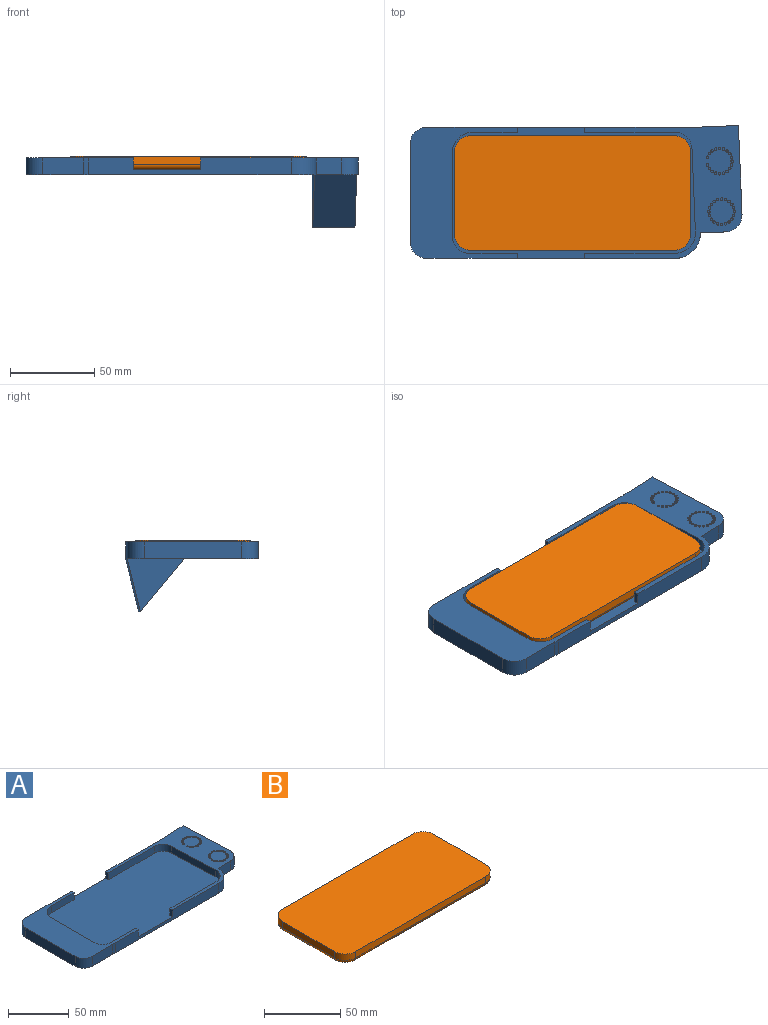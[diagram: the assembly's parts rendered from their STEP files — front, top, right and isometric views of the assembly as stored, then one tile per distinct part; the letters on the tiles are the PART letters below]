
ASSEMBLY  parts=2 mates=1
PART A: 118 faces, bbox 196.6x78.7x41.5 mm
  f0: cylinder r=0.75mm len=2mm, axis (0,0,1), area 9.4mm2, adj f1,f81
  f1: plane 1.5x1.5mm, normal (0,0,1), area 1.8mm2, adj f0
  f2: cylinder r=0.75mm len=2mm, axis (0,0,1), area 9.4mm2, adj f3,f81
  f3: plane 1.5x1.5mm, normal (0,0,1), area 1.8mm2, adj f2
  f4: cylinder r=0.75mm len=2mm, axis (0,0,1), area 9.4mm2, adj f5,f81
  f5: plane 1.5x1.5mm, normal (0,0,1), area 1.8mm2, adj f4
  f6: cylinder r=0.75mm len=2mm, axis (0,0,1), area 9.4mm2, adj f7,f81
  f7: plane 1.5x1.5mm, normal (0,0,1), area 1.8mm2, adj f6
  f8: cylinder r=0.75mm len=2mm, axis (0,0,1), area 9.4mm2, adj f9,f81
  f9: plane 1.5x1.5mm, normal (0,0,1), area 1.8mm2, adj f8
  f10: cylinder r=0.75mm len=2mm, axis (0,0,1), area 9.4mm2, adj f11,f81
  f11: plane 1.5x1.5mm, normal (0,0,1), area 1.8mm2, adj f10
  f12: cylinder r=0.75mm len=2mm, axis (0,0,1), area 9.4mm2, adj f13,f81
  f13: plane 1.5x1.5mm, normal (0,0,1), area 1.8mm2, adj f12
  f14: cylinder r=0.75mm len=2mm, axis (0,0,1), area 9.4mm2, adj f15,f81
  f15: plane 1.5x1.5mm, normal (0,0,1), area 1.8mm2, adj f14
  f16: cylinder r=0.75mm len=2mm, axis (0,0,1), area 9.4mm2, adj f17,f81
  f17: plane 1.5x1.5mm, normal (0,0,1), area 1.8mm2, adj f16
  f18: cylinder r=0.75mm len=2mm, axis (0,0,1), area 9.4mm2, adj f19,f81
  f19: plane 1.5x1.5mm, normal (0,0,1), area 1.8mm2, adj f18
  f20: cylinder r=0.75mm len=2mm, axis (0,0,1), area 9.4mm2, adj f21,f81
  f21: plane 1.5x1.5mm, normal (0,0,1), area 1.8mm2, adj f20
  f22: cylinder r=0.75mm len=2mm, axis (0,0,1), area 9.4mm2, adj f23,f81
  f23: plane 1.5x1.5mm, normal (0,0,1), area 1.8mm2, adj f22
  f24: cylinder r=0.75mm len=2mm, axis (0,0,1), area 9.4mm2, adj f25,f81
  f25: plane 1.5x1.5mm, normal (0,0,1), area 1.8mm2, adj f24
  f26: cylinder r=0.75mm len=2mm, axis (0,0,1), area 9.4mm2, adj f27,f81
  f27: plane 1.5x1.5mm, normal (0,0,1), area 1.8mm2, adj f26
  f28: cylinder r=0.75mm len=2mm, axis (0,0,1), area 9.4mm2, adj f29,f81
  f29: plane 1.5x1.5mm, normal (0,0,1), area 1.8mm2, adj f28
  f30: cylinder r=0.75mm len=2mm, axis (0,0,1), area 9.4mm2, adj f31,f81
  f31: plane 1.5x1.5mm, normal (0,0,1), area 1.8mm2, adj f30
  f32: cylinder r=0.75mm len=2mm, axis (0,0,1), area 9.4mm2, adj f33,f81
  f33: plane 1.5x1.5mm, normal (0,0,1), area 1.8mm2, adj f32
  f34: cylinder r=0.75mm len=2mm, axis (0,0,1), area 9.4mm2, adj f35,f81
  f35: plane 1.5x1.5mm, normal (0,0,1), area 1.8mm2, adj f34
  f36: cylinder r=0.75mm len=2mm, axis (0,0,1), area 9.4mm2, adj f37,f81
  f37: plane 1.5x1.5mm, normal (0,0,1), area 1.8mm2, adj f36
  f38: cylinder r=0.75mm len=2mm, axis (0,0,1), area 9.4mm2, adj f39,f81
  f39: plane 1.5x1.5mm, normal (0,0,1), area 1.8mm2, adj f38
  f40: cylinder r=0.75mm len=2mm, axis (0,0,1), area 9.4mm2, adj f41,f81
  f41: plane 1.5x1.5mm, normal (0,0,1), area 1.8mm2, adj f40
  f42: cylinder r=0.75mm len=2mm, axis (0,0,1), area 9.4mm2, adj f43,f81
  f43: plane 1.5x1.5mm, normal (0,0,1), area 1.8mm2, adj f42
  f44: cylinder r=0.75mm len=2mm, axis (0,0,1), area 9.4mm2, adj f45,f81
  f45: plane 1.5x1.5mm, normal (0,0,1), area 1.8mm2, adj f44
  f46: cylinder r=0.75mm len=2mm, axis (0,0,1), area 9.4mm2, adj f47,f81
  f47: plane 1.5x1.5mm, normal (0,0,1), area 1.8mm2, adj f46
  f48: cylinder r=0.75mm len=2mm, axis (0,0,1), area 9.4mm2, adj f49,f81
  f49: plane 1.5x1.5mm, normal (0,0,1), area 1.8mm2, adj f48
  f50: cylinder r=0.75mm len=2mm, axis (0,0,1), area 9.4mm2, adj f51,f81
  f51: plane 1.5x1.5mm, normal (0,0,1), area 1.8mm2, adj f50
  f52: cylinder r=0.75mm len=2mm, axis (0,0,1), area 9.4mm2, adj f53,f81
  f53: plane 1.5x1.5mm, normal (0,0,1), area 1.8mm2, adj f52
  f54: cylinder r=0.75mm len=2mm, axis (0,0,1), area 9.4mm2, adj f55,f81
  f55: plane 1.5x1.5mm, normal (0,0,1), area 1.8mm2, adj f54
  f56: cylinder r=0.75mm len=2mm, axis (0,0,1), area 9.4mm2, adj f57,f81
  f57: plane 1.5x1.5mm, normal (0,0,1), area 1.8mm2, adj f56
  f58: cylinder r=0.75mm len=2mm, axis (0,0,1), area 9.4mm2, adj f59,f81
  f59: plane 1.5x1.5mm, normal (0,0,1), area 1.8mm2, adj f58
  f60: cylinder r=0.75mm len=2mm, axis (0,0,1), area 9.4mm2, adj f61,f81
  f61: plane 1.5x1.5mm, normal (0,0,1), area 1.8mm2, adj f60
  f62: cylinder r=0.75mm len=2mm, axis (0,0,1), area 9.4mm2, adj f63,f81
  f63: plane 1.5x1.5mm, normal (0,0,1), area 1.8mm2, adj f62
  f64: cylinder r=0.75mm len=2mm, axis (0,0,1), area 9.4mm2, adj f65,f81
  f65: plane 1.5x1.5mm, normal (0,0,1), area 1.8mm2, adj f64
  f66: cylinder r=0.75mm len=2mm, axis (0,0,1), area 9.4mm2, adj f67,f81
  f67: plane 1.5x1.5mm, normal (0,0,1), area 1.8mm2, adj f66
  f68: cylinder r=0.75mm len=2mm, axis (0,0,1), area 9.4mm2, adj f69,f81
  f69: plane 1.5x1.5mm, normal (0,0,1), area 1.8mm2, adj f68
  f70: cylinder r=0.75mm len=2mm, axis (0,0,1), area 9.4mm2, adj f71,f81
  f71: plane 1.5x1.5mm, normal (0,0,1), area 1.8mm2, adj f70
  f72: cylinder r=0.75mm len=2mm, axis (0,0,1), area 9.4mm2, adj f73,f81
  f73: plane 1.5x1.5mm, normal (0,0,1), area 1.8mm2, adj f72
  f74: cylinder r=0.75mm len=2mm, axis (0,0,1), area 9.4mm2, adj f75,f81
  f75: plane 1.5x1.5mm, normal (0,0,1), area 1.8mm2, adj f74
  f76: plane 196.58x77.67mm, normal (0,0,-1), area 12261mm2, adj f77,f80,f90,f91,f92,f93,f94,f95
  f77: plane 41.49x33.96mm, normal (-1,-0.04,0), area 535.7mm2, adj f76,f81,f92,f112,f113,f114
  f78: plane 26.5x7mm, normal (0,-1,0), area 185.5mm2, adj f88,f97,f98,f99
  f79: plane 53.5x7mm, normal (0,1,0), area 374.5mm2, adj f81,f86,f98,f102
  f80: plane 120.16x10mm, normal (0,-1,0), area 921.6mm2, adj f76,f81,f90,f91,f97,f98,f101,f102
  f81: plane 93.08x78.66mm, normal (0,0,1), area 2096.1mm2, adj f0,f2,f4,f6,f8,f10,f12,f14
  f82: plane 49.6x7mm, normal (-1,-0.04,0), area 347.4mm2, adj f81,f86,f89,f98
  f83: plane 53.5x7mm, normal (0,-1,0), area 374.5mm2, adj f81,f89,f98,f100
  f84: plane 48.14x7mm, normal (1,0,0), area 337mm2, adj f87,f88,f97,f98
  f85: plane 26.83x7mm, normal (0,1,0), area 187.8mm2, adj f87,f97,f98,f101
  f86: cylinder r=12mm len=12mm, axis (0,0,-1), area 131.9mm2, adj f79,f81,f82,f98
  f87: cylinder r=10.48mm len=11.72mm, axis (0,0,-1), area 131.3mm2, adj f84,f85,f97,f98
  f88: cylinder r=12mm len=12mm, axis (0,0,-1), area 131.9mm2, adj f78,f84,f97,f98
  f89: cylinder r=10mm len=10mm, axis (0,0,-1), area 110mm2, adj f81,f82,f83,f98
  f90: cylinder r=13.48mm len=10mm, axis (0,0,-1), area 28.2mm2, adj f76,f80,f96,f97
  f91: cylinder r=15mm len=15.06mm, axis (0,0,-1), area 236.3mm2, adj f76,f80,f81,f110
  f92: plane 159.48x10mm, normal (0,1,0), area 1314.8mm2, adj f76,f77,f81,f93,f97,f98,f99,f100
  f93: cylinder r=10mm len=10mm, axis (0,0,-1), area 157.1mm2, adj f76,f92,f94,f97
  f94: plane 57.59x10mm, normal (-1,0,0), area 575.9mm2, adj f76,f93,f95,f97
  f95: cylinder r=10mm len=10mm, axis (0,0,-1), area 157.1mm2, adj f76,f94,f96,f97
  f96: plane 24.02x10mm, normal (0,-1,0), area 240.2mm2, adj f76,f90,f95,f97
  f97: plane 77.67x63.5mm, normal (0,0,1), area 2181.1mm2, adj f78,f80,f84,f85,f87,f88,f90,f92
  f98: plane 144.05x77.59mm, normal (0,0,1), area 10374.6mm2, adj f78,f79,f80,f82,f83,f84,f85,f86
  f99: plane 7x3mm, normal (1,0,0), area 21mm2, adj f78,f92,f97,f98
  f100: plane 7x3mm, normal (-1,0,0), area 21mm2, adj f81,f83,f92,f98
  f101: plane 7x3mm, normal (1,0,0), area 21mm2, adj f80,f85,f97,f98
  f102: plane 7x3mm, normal (-1,0,0), area 21mm2, adj f79,f80,f81,f98
  f103: plane 13.5x8.5mm, normal (0,-1,0), area 114.7mm2, adj f76,f104,f108,f109
  f104: plane 74.59x8.5mm, normal (-1,0,0), area 634mm2, adj f76,f103,f105,f109
  f105: plane 13.5x8.5mm, normal (0,1,0), area 114.7mm2, adj f76,f104,f106,f109
  f106: cylinder r=8.5mm len=8.5mm, axis (0,0,-1), area 113.5mm2, adj f76,f105,f107,f109
  f107: plane 57.59x8.5mm, normal (1,0,0), area 489.5mm2, adj f76,f106,f108,f109
  f108: cylinder r=8.5mm len=8.5mm, axis (0,0,-1), area 113.5mm2, adj f76,f103,f107,f109
  f109: plane 74.59x22mm, normal (0,0,-1), area 1610.1mm2, adj f103,f104,f105,f106,f107,f108
  f110: plane 14.99x10mm, normal (0.04,-1,0), area 150mm2, adj f76,f81,f91,f115
  f111: plane 52.59x41.49mm, normal (1,0.04,0), area 1061.5mm2, adj f76,f81,f112,f113,f114,f115
  f112: plane 24.98x10mm, normal (-0.04,1,0), area 250mm2, adj f77,f81,f111,f114
  f113: plane 31.49x27.16mm, normal (0.03,-0.77,-0.64), area 1023.7mm2, adj f76,f77,f111,f114
  f114: plane 31.49x25.29mm, normal (-0.04,0.97,-0.24), area 811.1mm2, adj f77,f111,f112,f113
  f115: cylinder r=10mm len=10.39mm, axis (0,0,1), area 157.1mm2, adj f76,f81,f110,f111
  f116: cylinder r=0.75mm len=2mm, axis (0,0,1), area 9.4mm2, adj f81,f117
  f117: plane 1.5x1.5mm, normal (0,0,1), area 1.8mm2, adj f116
PART B: 18 faces, bbox 141.6x69.6x8 mm
  f0: plane 48x5mm, normal (1,0,0), area 240mm2, adj f4,f6,f9,f16
  f1: plane 120x5mm, normal (0,1,0), area 600mm2, adj f4,f6,f7,f15
  f2: plane 48x5mm, normal (-1,0,0), area 240mm2, adj f4,f7,f8,f11
  f3: plane 120x5mm, normal (0,-1,0), area 600mm2, adj f4,f8,f9,f12
  f4: plane 140x68mm, normal (0,0,1), area 9434.2mm2, adj f0,f1,f2,f3,f6,f7,f8,f9
  f5: plane 134x62mm, normal (0,0,-1), area 8265.9mm2, adj f10,f11,f12,f13,f14,f15,f16,f17
  f6: cylinder r=10mm len=10mm, axis (0,0,1), area 78.5mm2, adj f0,f1,f4,f17
  f7: cylinder r=10mm len=10mm, axis (0,0,-1), area 78.5mm2, adj f1,f2,f4,f13
  f8: cylinder r=10mm len=10mm, axis (0,0,1), area 78.5mm2, adj f2,f3,f4,f10
  f9: cylinder r=10mm len=10mm, axis (0,0,-1), area 78.5mm2, adj f0,f3,f4,f14
  f10: torus R=7mm, axis (0,0,1), area 66mm2, adj f5,f8,f11,f12
  f11: cylinder r=3mm len=48mm, axis (0,-1,0), area 226.2mm2, adj f2,f5,f10,f13
  f12: cylinder r=3mm len=120mm, axis (1,0,0), area 565.5mm2, adj f3,f5,f10,f14
  f13: torus R=7mm, axis (0,0,1), area 66mm2, adj f5,f7,f11,f15
  f14: torus R=7mm, axis (0,0,1), area 66mm2, adj f5,f9,f12,f16
  f15: cylinder r=3mm len=120mm, axis (-1,0,0), area 565.5mm2, adj f1,f5,f13,f17
  f16: cylinder r=3mm len=48mm, axis (0,1,0), area 226.2mm2, adj f0,f5,f14,f17
  f17: torus R=7mm, axis (0,0,1), area 66mm2, adj f5,f6,f15,f16
PLACE A t=(-24.34,-9.58,-12.5)mm
PLACE B t=(-78.33,-60.11,-9.5)mm
MATE planar B.f5 <-> A.f98  axis (0,0,-1) through (-78.33,-60.11,-9.5)mm
